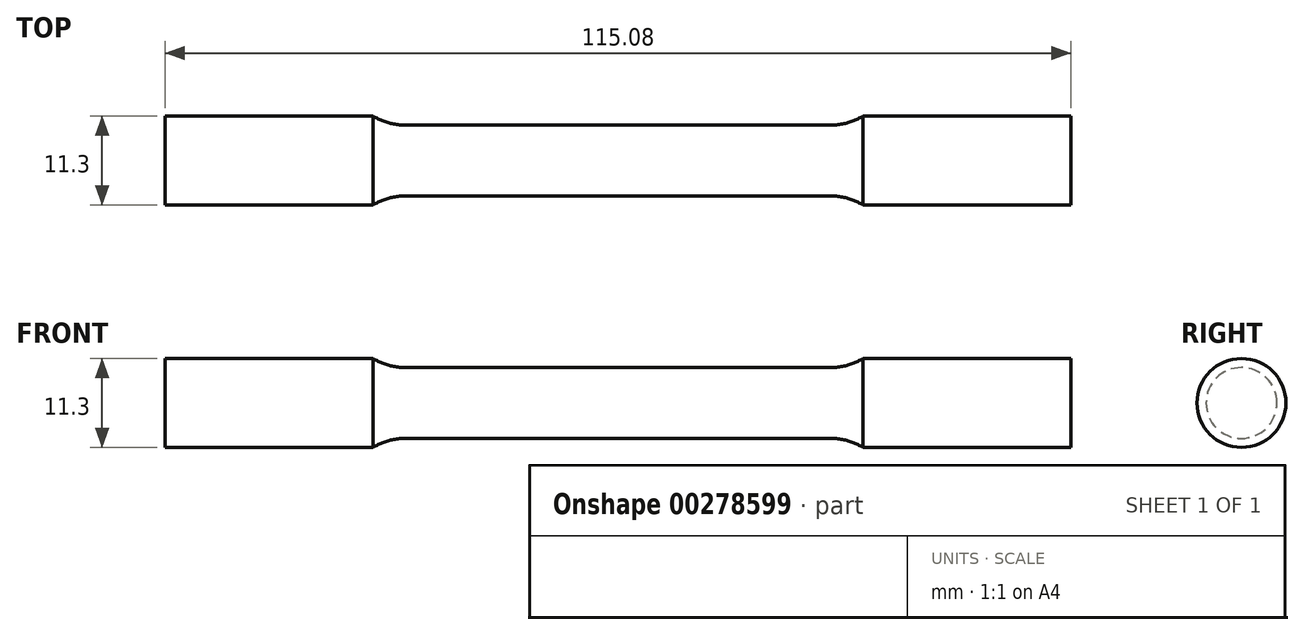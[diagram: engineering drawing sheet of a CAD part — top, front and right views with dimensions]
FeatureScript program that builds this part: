
annotation { "Feature Type Name" : "Feature", "Feature Type Description" : "" }
export const myFeature = defineFeature(function(context is Context, id is Id, definition is map)
    precondition{}
    {
        {
            var Q0;
            Q0=qCreatedBy(makeId("Front.planeOp"),FACE);
            var sketch = newSketch(context, id + "F0", { "sketchPlane" : qUnion([Q0])});
            skLineSegment(sketch, "E0", {"start": v(0, 4.5) * mm, "end": v(27, 4.5) * mm});
            skArc(sketch, "E1", {"start": v(27, 4.5) * mm, "mid": v(29.14, 4.8) * mm, "end": v(31.13, 5.65) * mm});
            skLineSegment(sketch, "E2", {"start": v(31.13, 5.65) * mm, "end": v(57.54, 5.65) * mm});
            skLineSegment(sketch, "E3", {"start": v(57.54, 5.65) * mm, "end": v(57.54, 0) * mm});
            skLineSegment(sketch, "E4.MirrorCS", {"start": v(0, 4.5) * mm, "end": v(-27, 4.5) * mm});
            skLineSegment(sketch, "E5.MirrorCS", {"start": v(-57.54, 5.65) * mm, "end": v(-57.54, 0) * mm});
            skLineSegment(sketch, "E6.MirrorCS", {"start": v(-31.13, 5.65) * mm, "end": v(-57.54, 5.65) * mm});
            skArc(sketch, "E7.MirrorCS", {"start": v(-27, 4.5) * mm, "mid": v(-29.14, 4.8) * mm, "end": v(-31.13, 5.65) * mm});
            skLineSegment(sketch, "E8", {"start": v(-57.54, 0) * mm, "end": v(57.54, 0) * mm});
            skSolve(sketch);
        }
        {
            var Q0;
            Q0 = qSketchRegion(id + "F0", true);
            var Q1;
            Q1=sQuery(id+"F0.wireOp",EDGE,"E8");
            revolve(context, id + "F1", {"entities" : qUnion([Q0]), "axis" : qUnion([Q1]), "revolveType" : RevolveType.FULL});
        }
    });
